# Revit family: QF_Vivreau_PURITY C150 Quell ST
name_source: partatom
category: Specialty Equipment
revit_build: Autodesk Revit 2018 (Build: 20190510_1515(x64)
units: mm (PartAtom-declared; Revit-internal decimal feet)

## family parameters
Always vertical = Yes
Cut with Voids When Loaded = No
OmniClass Number = 23.40.40.14.24
OmniClass Title = Food Dispensing Equipment
Part Type = Normal
Room Calculation Point = No
Round Connector Dimension = Use Diameter
Shared = No
Work Plane-Based = No

## types (1)
- QF_Vivreau_PURITY C150 Quell ST
    Assembly Code = E1090320
    CSI MasterFormat = 11 46 00
    Cold Water Connection Height = 1' - 3 1/2"
    Cold Water Flow = 0.264 GPM
    Cold Water Maximum Pressure = 124.00 psi
    Cold Water Minimum Pressure = 29.00 psi
    Cold Water RI Height = 0' - 0"
    Cold Water Size = 1"
    Cold Water Temperature Recommended = 40 °F
    Depth = 0' - 4 1/4"
    Description = Water Filter
    Foodservice Equipment Identifier = Yes
    Height = 1' - 4 13/32"
    Identify Quantity as Lot = Yes
    Manufacturer = Vivreau
    Masterspec = Division 11
    Model = PURITY C150 Quell ST
    Plumbing Connection Type = NPT
    URL = www.vivreauwater.com/professional-filters
    Weight in Pounds = 3.96
    Width = 0' - 4 3/32"

## geometry (parser evidence)
native form markers: Sweep x10
no freeform markers — native parametric forms only
